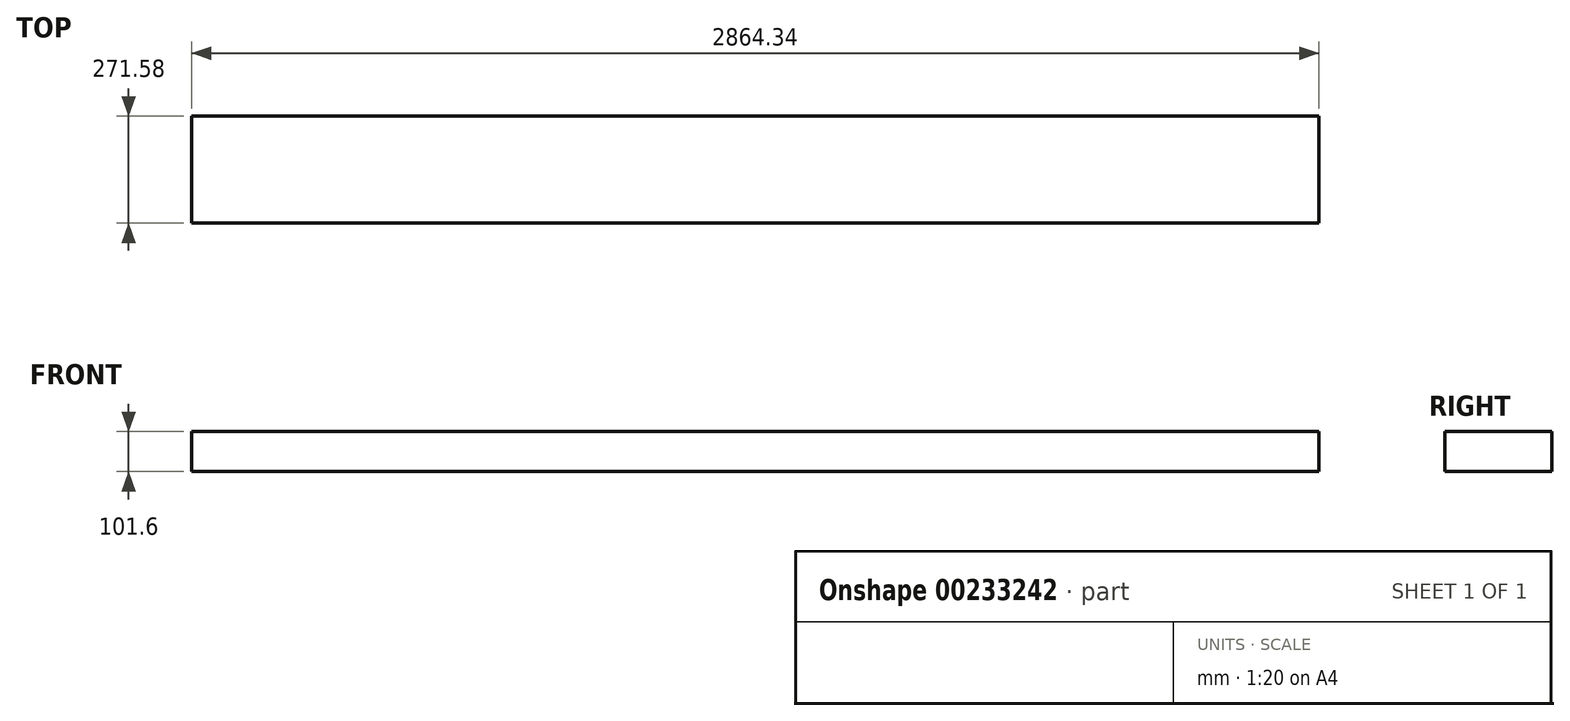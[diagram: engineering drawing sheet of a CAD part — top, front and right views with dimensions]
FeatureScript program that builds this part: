
annotation { "Feature Type Name" : "Feature", "Feature Type Description" : "" }
export const myFeature = defineFeature(function(context is Context, id is Id, definition is map)
    precondition{}
    {
        {
            var Q0;
            Q0=qCreatedBy(makeId("Top.planeOp"),FACE);
            var sketch = newSketch(context, id + "F0", { "sketchPlane" : qUnion([Q0])});
            skLineSegment(sketch, "E0.bottom", {"start": v(110.85, -2346.14) * mm, "end": v(2975.19, -2346.14) * mm});
            skLineSegment(sketch, "E0.top", {"start": v(110.85, -2617.72) * mm, "end": v(2975.19, -2617.72) * mm});
            skLineSegment(sketch, "E0.left", {"start": v(110.85, -2346.14) * mm, "end": v(110.85, -2617.72) * mm});
            skLineSegment(sketch, "E0.right", {"start": v(2975.19, -2346.14) * mm, "end": v(2975.19, -2617.72) * mm});
            skSolve(sketch);
        }
        {
            var Q0;
            Q0=makeQuery(id+"F0.imprint","IMPRINT",FACE,{"disambiguationData":[TD([[makeQuery(id+"F0.imprint","IMPRINT",EDGE,{"derivedFrom":sQuery(id+"F0.wireOp",EDGE,"E0.bottom")}),-1.0]])]});
            extrude(context, id + "F1", {"entities" : qUnion([Q0]), "depth" : 101.6 * mm});
        }
    });
